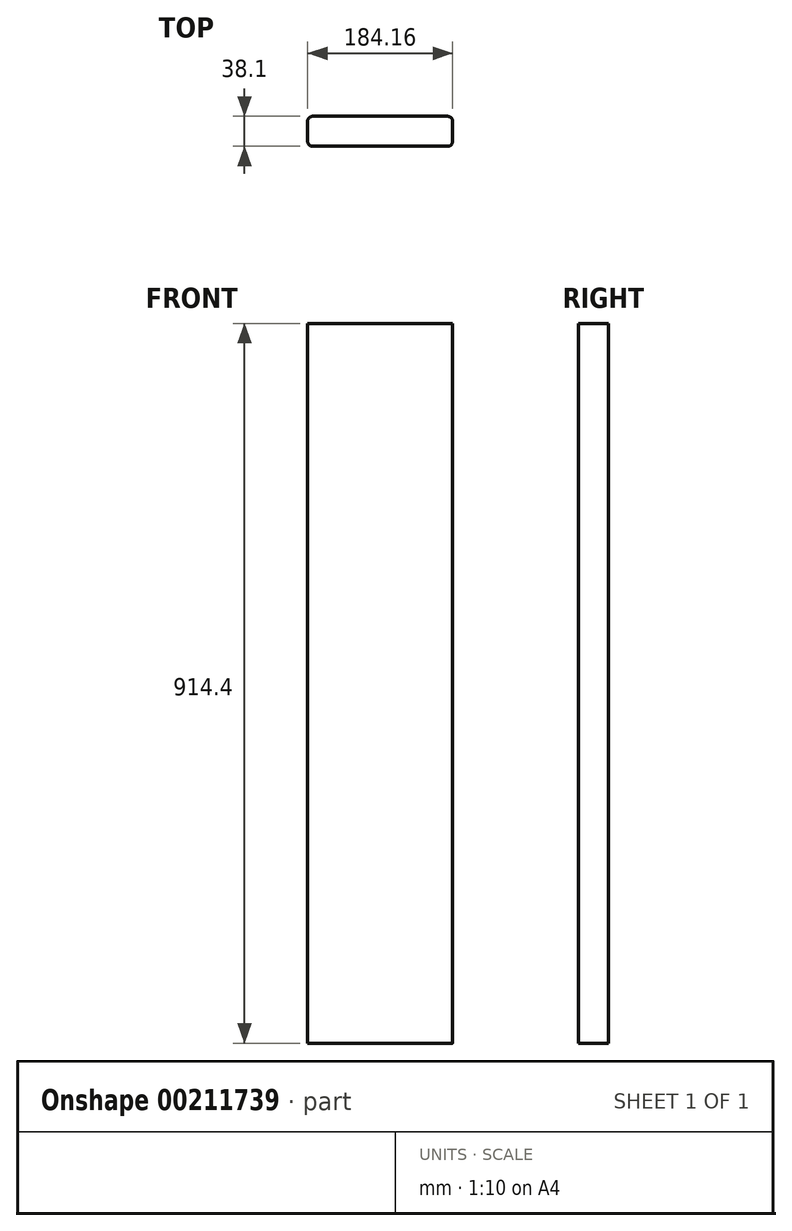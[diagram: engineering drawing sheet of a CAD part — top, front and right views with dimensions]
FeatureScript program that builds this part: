
annotation { "Feature Type Name" : "Feature", "Feature Type Description" : "" }
export const myFeature = defineFeature(function(context is Context, id is Id, definition is map)
    precondition{}
    {
        {
            var Q0;
            Q0=qCreatedBy(makeId("Front.planeOp"),FACE);
            var sketch = newSketch(context, id + "F0", { "sketchPlane" : qUnion([Q0])});
            skLineSegment(sketch, "E0.bottom", {"start": v(-92.08, 457.2) * mm, "end": v(92.08, 457.2) * mm});
            skLineSegment(sketch, "E0.top", {"start": v(-92.08, -457.2) * mm, "end": v(92.08, -457.2) * mm});
            skLineSegment(sketch, "E0.left", {"start": v(-92.08, 457.2) * mm, "end": v(-92.08, -457.2) * mm});
            skLineSegment(sketch, "E0.right", {"start": v(92.08, 457.2) * mm, "end": v(92.08, -457.2) * mm});
            skSolve(sketch);
        }
        {
            var Q0;
            Q0=makeQuery(id+"F0.imprint","IMPRINT",FACE,{"disambiguationData":[TD([[makeQuery(id+"F0.imprint","IMPRINT",EDGE,{"derivedFrom":sQuery(id+"F0.wireOp",EDGE,"E0.bottom")}),-1.0]])]});
            extrude(context, id + "F1", {"entities" : qUnion([Q0]), "depth" : 38.1 * mm});
        }
        {
            var Q0;
            Q0=makeQuery(id+"F1.opExtrude","CAP_EDGE",EDGE,{"disambiguationData":[OSD([sQuery(id+"F0.wireOp",EDGE,"E0.right")])],"isStart":false});
            var Q1;
            Q1=makeQuery(id+"F1.opExtrude","CAP_EDGE",EDGE,{"disambiguationData":[OSD([sQuery(id+"F0.wireOp",EDGE,"E0.right")])],"isStart":true});
            var Q2;
            Q2=makeQuery(id+"F1.opExtrude","CAP_EDGE",EDGE,{"disambiguationData":[OSD([sQuery(id+"F0.wireOp",EDGE,"E0.left")])],"isStart":false});
            var Q3;
            Q3=makeQuery(id+"F1.opExtrude","CAP_EDGE",EDGE,{"disambiguationData":[OSD([sQuery(id+"F0.wireOp",EDGE,"E0.left")])],"isStart":true});
            fillet(context, id + "F2", {"entities" : qUnion([Q0, Q1, Q2, Q3]), "radius" : 6.35 * mm, "tangentPropagation" : true, "allowEdgeOverflow" : false});
        }
    });
